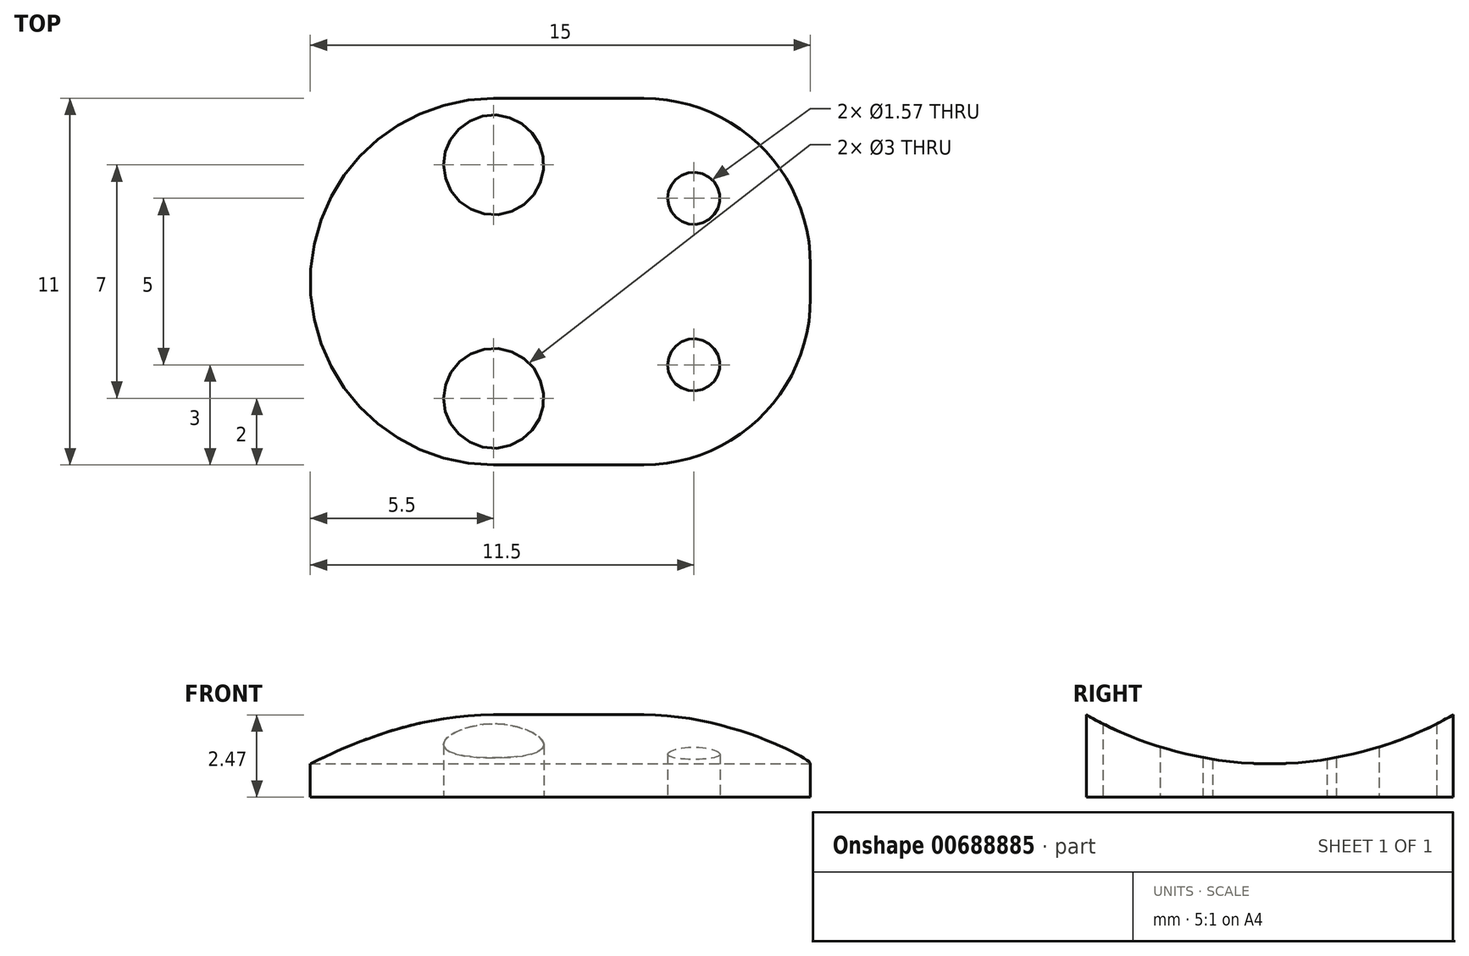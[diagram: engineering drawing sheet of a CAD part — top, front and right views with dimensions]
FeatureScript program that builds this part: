
annotation { "Feature Type Name" : "Feature", "Feature Type Description" : "" }
export const myFeature = defineFeature(function(context is Context, id is Id, definition is map)
    precondition{}
    {
        {
            var Q0;
            Q0=qCreatedBy(makeId("Top.planeOp"),FACE);
            var sketch = newSketch(context, id + "F0", { "sketchPlane" : qUnion([Q0])});
            skFitSpline(sketch, "E0.0.0", {"points": [v(9.5, -0.5) * mm, v(9.5, -0.17) * mm, v(9.5, 0.17) * mm, v(9.5, 0.5) * mm]});
            skFitSpline(sketch, "E0.0.1", {"points": [v(9.5, 0.5) * mm, v(9.5, 0.83) * mm, v(9.47, 1.15) * mm, v(9.4, 1.48) * mm, v(9.34, 1.8) * mm, v(9.24, 2.11) * mm, v(9.12, 2.41) * mm, v(9, 2.72) * mm, v(8.84, 3) * mm, v(8.66, 3.28) * mm, v(8.47, 3.55) * mm, v(8.27, 3.8) * mm, v(8.04, 4.04) * mm, v(7.8, 4.27) * mm, v(7.55, 4.48) * mm, v(7.28, 4.66) * mm, v(7, 4.84) * mm, v(6.72, 5) * mm, v(6.41, 5.12) * mm, v(6.1, 5.25) * mm, v(5.8, 5.34) * mm, v(5.48, 5.4) * mm, v(5.15, 5.47) * mm, v(4.83, 5.5) * mm, v(4.5, 5.5) * mm]});
            skFitSpline(sketch, "E0.0.2", {"points": [v(4.5, 5.5) * mm, v(3, 5.5) * mm, v(1.5, 5.5) * mm, v(0, 5.5) * mm]});
            skFitSpline(sketch, "E0.0.3", {"points": [v(0, 5.5) * mm, v(-0.36, 5.5) * mm, v(-0.72, 5.46) * mm, v(-1.07, 5.4) * mm, v(-1.43, 5.32) * mm, v(-1.77, 5.22) * mm, v(-2.1, 5.08) * mm, v(-2.44, 4.94) * mm, v(-2.76, 4.77) * mm, v(-3.06, 4.57) * mm, v(-3.36, 4.37) * mm, v(-3.63, 4.14) * mm, v(-3.89, 3.89) * mm, v(-4.14, 3.63) * mm, v(-4.37, 3.36) * mm, v(-4.57, 3.06) * mm, v(-4.77, 2.76) * mm, v(-4.94, 2.44) * mm, v(-5.08, 2.1) * mm, v(-5.22, 1.77) * mm, v(-5.32, 1.43) * mm, v(-5.4, 1.07) * mm, v(-5.46, 0.72) * mm, v(-5.5, 0.36) * mm, v(-5.5, 0) * mm, v(-5.5, -0.36) * mm, v(-5.46, -0.72) * mm, v(-5.4, -1.07) * mm, v(-5.32, -1.43) * mm, v(-5.22, -1.77) * mm, v(-5.08, -2.1) * mm, v(-4.94, -2.44) * mm, v(-4.77, -2.76) * mm, v(-4.57, -3.06) * mm, v(-4.37, -3.36) * mm, v(-4.14, -3.63) * mm, v(-3.89, -3.89) * mm, v(-3.63, -4.14) * mm, v(-3.36, -4.37) * mm, v(-3.06, -4.57) * mm, v(-2.76, -4.77) * mm, v(-2.44, -4.94) * mm, v(-2.1, -5.08) * mm, v(-1.77, -5.22) * mm, v(-1.43, -5.32) * mm, v(-1.07, -5.4) * mm, v(-0.72, -5.46) * mm, v(-0.36, -5.5) * mm, v(0, -5.5) * mm]});
            skFitSpline(sketch, "E0.0.4", {"points": [v(0, -5.5) * mm, v(1.5, -5.5) * mm, v(3, -5.5) * mm, v(4.5, -5.5) * mm]});
            skFitSpline(sketch, "E0.0.5", {"points": [v(4.5, -5.5) * mm, v(4.83, -5.5) * mm, v(5.15, -5.47) * mm, v(5.48, -5.4) * mm, v(5.8, -5.34) * mm, v(6.11, -5.24) * mm, v(6.41, -5.12) * mm, v(6.72, -5) * mm, v(7, -4.84) * mm, v(7.28, -4.66) * mm, v(7.55, -4.47) * mm, v(7.8, -4.27) * mm, v(8.04, -4.04) * mm, v(8.27, -3.8) * mm, v(8.48, -3.55) * mm, v(8.66, -3.28) * mm, v(8.84, -3) * mm, v(9, -2.72) * mm, v(9.12, -2.41) * mm, v(9.25, -2.1) * mm, v(9.34, -1.8) * mm, v(9.4, -1.48) * mm, v(9.47, -1.15) * mm, v(9.5, -0.83) * mm, v(9.5, -0.5) * mm]});
            skCircle(sketch, "E1.0", {"center": v(6, 2.5) * mm, "radius": 0.78 * mm});
            skCircle(sketch, "E2.0", {"center": v(6, -2.5) * mm, "radius": 0.78 * mm});
            skFitSpline(sketch, "E3.0", {"points": [v(1.42, -4.09) * mm, v(1.54, -3.5) * mm, v(1.42, -2.91) * mm, v(1.09, -2.41) * mm, v(0.59, -2.08) * mm, v(0, -1.96) * mm, v(-0.59, -2.08) * mm, v(-1.09, -2.41) * mm, v(-1.42, -2.91) * mm, v(-1.54, -3.5) * mm, v(-1.42, -4.09) * mm, v(-1.09, -4.59) * mm, v(-0.59, -4.92) * mm, v(0, -5.04) * mm, v(0.59, -4.92) * mm, v(1.09, -4.59) * mm, v(1.42, -4.09) * mm, v(1.54, -3.5) * mm, v(1.42, -2.91) * mm, v(1.42, -4.09) * mm]});
            skFitSpline(sketch, "E4.0", {"points": [v(0.63, -2.87) * mm, v(0.89, -3.5) * mm, v(0.63, -4.13) * mm, v(0, -4.39) * mm, v(-0.63, -4.13) * mm, v(-0.89, -3.5) * mm, v(-0.63, -2.87) * mm, v(0, -2.61) * mm, v(0.63, -2.87) * mm, v(0.89, -3.5) * mm, v(0.63, -4.13) * mm, v(0.63, -2.87) * mm]});
            skFitSpline(sketch, "E5.0", {"points": [v(1.42, 2.91) * mm, v(1.54, 3.5) * mm, v(1.42, 4.09) * mm, v(1.09, 4.59) * mm, v(0.59, 4.92) * mm, v(0, 5.04) * mm, v(-0.59, 4.92) * mm, v(-1.09, 4.59) * mm, v(-1.42, 4.09) * mm, v(-1.54, 3.5) * mm, v(-1.42, 2.91) * mm, v(-1.09, 2.41) * mm, v(-0.59, 2.08) * mm, v(0, 1.96) * mm, v(0.59, 2.08) * mm, v(1.09, 2.41) * mm, v(1.42, 2.91) * mm, v(1.54, 3.5) * mm, v(1.42, 4.09) * mm, v(1.42, 2.91) * mm]});
            skFitSpline(sketch, "E6.0", {"points": [v(0.63, 4.13) * mm, v(0.89, 3.5) * mm, v(0.63, 2.87) * mm, v(0, 2.61) * mm, v(-0.63, 2.87) * mm, v(-0.89, 3.5) * mm, v(-0.63, 4.13) * mm, v(0, 4.39) * mm, v(0.63, 4.13) * mm, v(0.89, 3.5) * mm, v(0.63, 2.87) * mm, v(0.63, 4.13) * mm]});
            skPoint(sketch, "E7.0", {"position": v(0, 0) * mm});
            skLineSegment(sketch, "E8", {"start": v(4.5, 5.5) * mm, "end": v(0, 5.5) * mm});
            skLineSegment(sketch, "E9", {"start": v(4.5, -5.5) * mm, "end": v(0, -5.5) * mm});
            skArc(sketch, "E10", {"start": v(0, 5.5) * mm, "mid": v(-5.5, 0) * mm, "end": v(0, -5.5) * mm});
            skArc(sketch, "E11", {"start": v(9.5, 0.5) * mm, "mid": v(8.04, 4.04) * mm, "end": v(4.5, 5.5) * mm});
            skArc(sketch, "E12", {"start": v(4.5, -5.5) * mm, "mid": v(8.04, -4.04) * mm, "end": v(9.5, -0.5) * mm});
            skCircle(sketch, "E13", {"center": v(0, 3.5) * mm, "radius": 0.8 * mm});
            skPoint(sketch, "E13.first.point", {"position": v(-0.44, 4.16) * mm});
            skPoint(sketch, "E13.second.point", {"position": v(-0.33, 2.77) * mm});
            skPoint(sketch, "E13.third.point", {"position": v(0.8, 3.6) * mm});
            skCircle(sketch, "E14", {"center": v(0, 3.5) * mm, "radius": 1.5 * mm});
            skCircle(sketch, "E15", {"center": v(0, -3.5) * mm, "radius": 0.8 * mm});
            skPoint(sketch, "E15.first.point", {"position": v(-0.63, -3) * mm});
            skPoint(sketch, "E15.second.point", {"position": v(-0.23, -4.27) * mm});
            skPoint(sketch, "E15.third.point", {"position": v(0.78, -3.32) * mm});
            skCircle(sketch, "E16", {"center": v(0, -3.5) * mm, "radius": 1.5 * mm});
            skSolve(sketch);
        }
        {
            var Q0;
            Q0=makeQuery(id+"F0.imprint","IMPRINT",FACE,{"disambiguationData":[TD([[makeQuery(id+"F0.imprint","IMPRINT",EDGE,{"derivedFrom":sQuery(id+"F0.wireOp",EDGE,"E0.0.0")}),1.0]])]});
            var Q1;
            Q1=makeQuery(id+"F0.imprint","IMPRINT",FACE,{"disambiguationData":[TD([[makeQuery(id+"F0.imprint","IMPRINT",EDGE,{"derivedFrom":sQuery(id+"F0.wireOp",EDGE,"E5.0")}),1.0]])]});
            var Q2;
            {var subQ15=sQuery(id+"F0.wireOp",EDGE,"E16");var subQ16=sQuery(id+"F0.wireOp",EDGE,"E3.0");var subQ17=makeQuery(id+"F0.imprint","INTERSECT",VERTEX,{"disambiguationData":[OD(0.0)],"derivedFrom":[subQ16,subQ15]});Q2=makeQuery(id+"F0.imprint","IMPRINT",FACE,{"disambiguationData":[TD([[makeQuery(id+"F0.imprint","IMPRINT",EDGE,{"disambiguationData":[TD([[subQ17,1.0]])],"derivedFrom":subQ16}),1.0]])]});}
            extrude(context, id + "F1", {"entities" : qUnion([Q0, Q1, Q2]), "depth" : 5 * mm, "offsetDistance" : 25.4 * mm});
        }
        {
            var Q0;
            Q0=qCreatedBy(makeId("Right.planeOp"),FACE);
            var sketch = newSketch(context, id + "F2", { "sketchPlane" : qUnion([Q0])});
            skCircle(sketch, "E17", {"center": v(0, 12) * mm, "radius": 11 * mm});
            skSolve(sketch);
        }
        {
            var Q0;
            Q0=makeQuery(id+"F2.imprint","IMPRINT",FACE,{"disambiguationData":[TD([[makeQuery(id+"F2.imprint","IMPRINT",EDGE,{"derivedFrom":sQuery(id+"F2.wireOp",EDGE,"E17")}),1.0]])]});
            extrude(context, id + "F3", {"entities" : qUnion([Q0]), "operationType" : NewBodyOperationType.REMOVE, "endBound" : BoundingType.SYMMETRIC, "oppositeDirection" : true, "depth" : 20 * mm, "offsetDistance" : 25 * mm});
        }
    });
